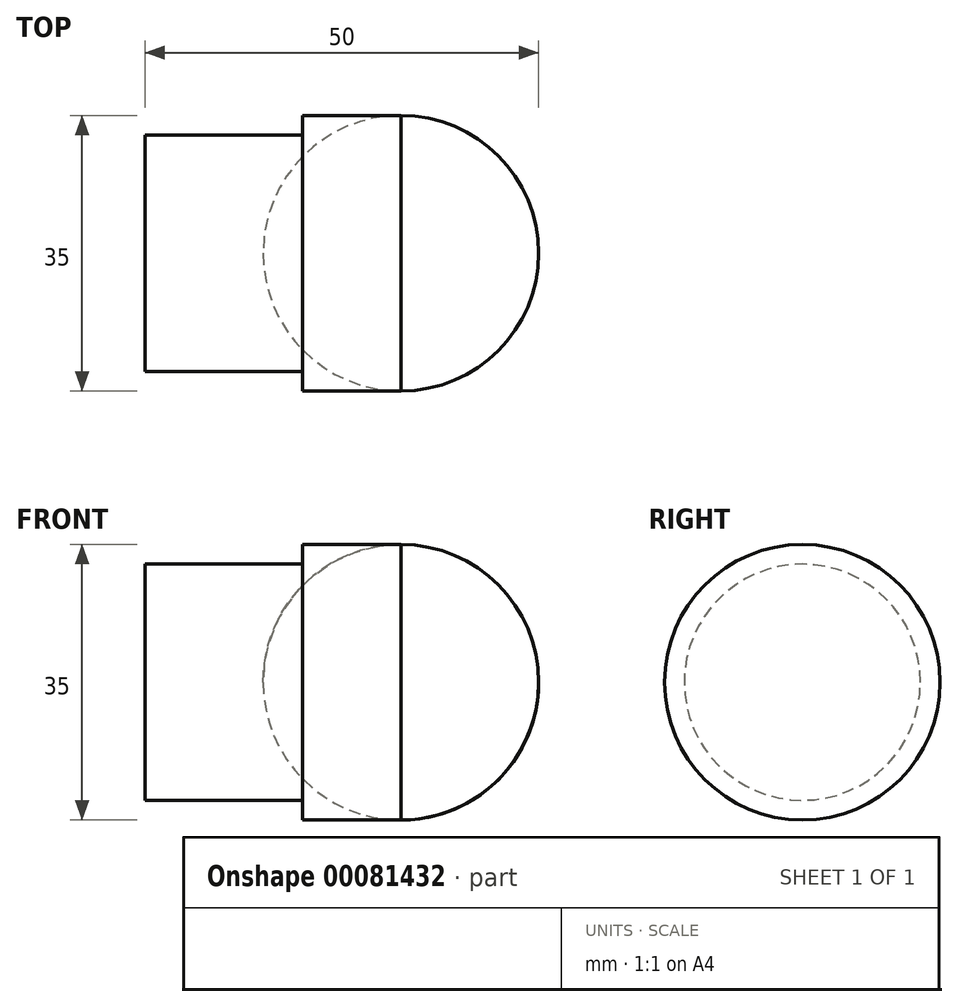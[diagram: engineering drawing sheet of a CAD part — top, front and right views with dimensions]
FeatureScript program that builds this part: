
annotation { "Feature Type Name" : "Feature", "Feature Type Description" : "" }
export const myFeature = defineFeature(function(context is Context, id is Id, definition is map)
    precondition{}
    {
        {
            var Q0;
            Q0=qCreatedBy(makeId("Front.planeOp"),FACE);
            var sketch = newSketch(context, id + "F0", { "sketchPlane" : qUnion([Q0])});
            skLineSegment(sketch, "E0", {"start": v(28.19, 0) * mm, "end": v(-61.9, 0) * mm, "construction": true});
            skCircle(sketch, "E1", {"center": v(0, 0) * mm, "radius": 17.5 * mm});
            skLineSegment(sketch, "E2.bottom", {"start": v(0, 17.5) * mm, "end": v(-12.5, 17.5) * mm});
            skLineSegment(sketch, "E2.top", {"start": v(0, -17.5) * mm, "end": v(-12.5, -17.5) * mm});
            skLineSegment(sketch, "E2.left", {"start": v(0, 17.5) * mm, "end": v(0, -17.5) * mm});
            skLineSegment(sketch, "E2.right", {"start": v(-12.5, 17.5) * mm, "end": v(-12.5, -17.5) * mm});
            skLineSegment(sketch, "E3.bottom", {"start": v(-12.5, 15) * mm, "end": v(-32.5, 15) * mm});
            skLineSegment(sketch, "E3.top", {"start": v(-12.5, -15) * mm, "end": v(-32.5, -15) * mm});
            skLineSegment(sketch, "E3.left", {"start": v(-12.5, 15) * mm, "end": v(-12.5, -15) * mm});
            skLineSegment(sketch, "E3.right", {"start": v(-32.5, 15) * mm, "end": v(-32.5, -15) * mm});
            skLineSegment(sketch, "E4", {"start": v(-32.5, 15) * mm, "end": v(-12.5, -15) * mm, "construction": true});
            skLineSegment(sketch, "E5", {"start": v(-32.5, 0) * mm, "end": v(-12.5, 0) * mm, "construction": true});
            skLineSegment(sketch, "E6", {"start": v(-37.78, 0) * mm, "end": v(24.6, 0) * mm});
            skSolve(sketch);
        }
        {
            var Q0;
            {var subQ1=sQuery(id+"F0.wireOp",EDGE,"E3.bottom");Q0=makeQuery(id+"F0.imprint","IMPRINT",FACE,{"disambiguationData":[TD([[makeQuery(id+"F0.imprint","IMPRINT",EDGE,{"derivedFrom":subQ1}),1.0]])]});}
            var Q1;
            {var subQ0=sQuery(id+"F0.wireOp",EDGE,"E3.left");var subQ1=sQuery(id+"F0.wireOp",EDGE,"E1");var subQ2=makeQuery(id+"F0.imprint","INTERSECT",VERTEX,{"disambiguationData":[OD(0.0)],"derivedFrom":[subQ1,subQ0]});Q1=makeQuery(id+"F0.imprint","IMPRINT",FACE,{"disambiguationData":[TD([[makeQuery(id+"F0.imprint","IMPRINT",EDGE,{"disambiguationData":[TD([[subQ2,-1.0]])],"derivedFrom":subQ1}),1.0]])]});}
            var Q2;
            {var subQ0=sQuery(id+"F0.wireOp",EDGE,"E2.bottom");Q2=makeQuery(id+"F0.imprint","IMPRINT",FACE,{"disambiguationData":[TD([[makeQuery(id+"F0.imprint","IMPRINT",EDGE,{"derivedFrom":subQ0}),1.0]])]});}
            var Q3;
            {var subQ1=sQuery(id+"F0.wireOp",EDGE,"E1");var subQ3=sQuery(id+"F0.wireOp",EDGE,"E3.left");var subQ4=makeQuery(id+"F0.imprint","INTERSECT",VERTEX,{"disambiguationData":[OD(0.0)],"derivedFrom":[subQ1,subQ3]});Q3=makeQuery(id+"F0.imprint","IMPRINT",FACE,{"disambiguationData":[TD([[makeQuery(id+"F0.imprint","IMPRINT",EDGE,{"disambiguationData":[TD([[subQ4,-1.0]])],"derivedFrom":subQ3}),1.0]])]});}
            var Q4;
            {var subQ1=sQuery(id+"F0.wireOp",EDGE,"E1");var subQ3=sQuery(id+"F0.wireOp",EDGE,"E6");var subQ4=makeQuery(id+"F0.imprint","INTERSECT",VERTEX,{"disambiguationData":[OD(0.0)],"derivedFrom":[subQ1,subQ3]});Q4=makeQuery(id+"F0.imprint","IMPRINT",FACE,{"disambiguationData":[TD([[makeQuery(id+"F0.imprint","IMPRINT",EDGE,{"disambiguationData":[TD([[subQ4,1.0]])],"derivedFrom":subQ3}),1.0]])]});}
            var Q5;
            Q5=sQuery(id+"F0.wireOp",EDGE,"E0");
            revolve(context, id + "F1", {"entities" : qUnion([Q0, Q1, Q2, Q3, Q4]), "axis" : qUnion([Q5]), "revolveType" : RevolveType.FULL});
        }
    });
